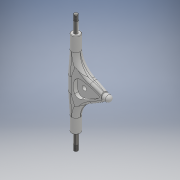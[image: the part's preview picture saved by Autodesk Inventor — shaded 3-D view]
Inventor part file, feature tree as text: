
AUTODESK INVENTOR PART (.ipt)
format: ipt  version: 2018 (Build 220112000, 112)  size: 434,176 bytes
history: native  units: mm
features: extrude x12, sketch x11, chamfer x7, fillet x5, other x3, thread x2
ambient origin geometry x8: Origin, YZ Plane, XZ Plane, XY Plane, X Axis, Y Axis, Z Axis, Center Point
bodies: Body1 (feature_tree)
feature tree (40):
  other  "Твердое тело1"
  sketch  "Эскиз1"
  extrude  "Выдавливание1"  Depth=18.0mm
  extrude  "Выдавливание2"  Depth=180.0mm TaperAngle=0.0deg
  chamfer  "Фаска1"  Distance=23.0mm
  chamfer  "Фаска2"  Distance=30.0mm
  sketch  "Эскиз2"
  extrude  "Выдавливание3"  Depth=45.0mm TaperAngle=45.0deg
  extrude  "Выдавливание4"  Depth=45.0mm TaperAngle=45.0deg
  extrude  "Выдавливание5"  Depth=8.0mm
  extrude  "Выдавливание6"  Depth=35.0mm TaperAngle=0.0deg
  chamfer  "Фаска3"  Distance=35.0mm
  fillet  "Сопряжение1"  Radius=0.1mm
  sketch  "Эскиз6"
  other  "РабПлоскость3"
  extrude  "Выдавливание10"  Depth=12.0mm TaperAngle=0.0deg
  chamfer  "Фаска4"  Distance=12.0mm
  chamfer  "Фаска5"  Distance=0.5mm Angle=45.0deg
  chamfer  "Фаска6"  Distance=1.0mm
  chamfer  "Фаска7"  Distance=68.0mm
  extrude  "Выдавливание12"  Depth=140.0mm
  fillet  "Сопряжение7"  Radius=108.0mm
  fillet  "Сопряжение8"  Radius=18.0mm
  extrude  "Выдавливание13"  Depth=23.0mm TaperAngle=0.0deg
  fillet  "Сопряжение9"  Radius=45.0mm
  extrude  "Выдавливание14"  Depth=45.0mm TaperAngle=45.0deg
  fillet  "Сопряжение11"  Radius=45.0mm
  extrude  "Выдавливание15"  Depth=45.0mm TaperAngle=45.0deg
  thread  "Резьба1"
  thread  "Резьба2"
  other  "РабПлоскость4"
  extrude  "Выдавливание16"  Depth=14.0mm
  sketch  "Эскиз3"
  sketch  "Эскиз4"
  sketch  "Эскиз5"
  sketch  "Эскиз22"
  sketch  "Эскиз23"
  sketch  "Эскиз24"
  sketch  "Эскиз25"
  sketch  "Эскиз26"
